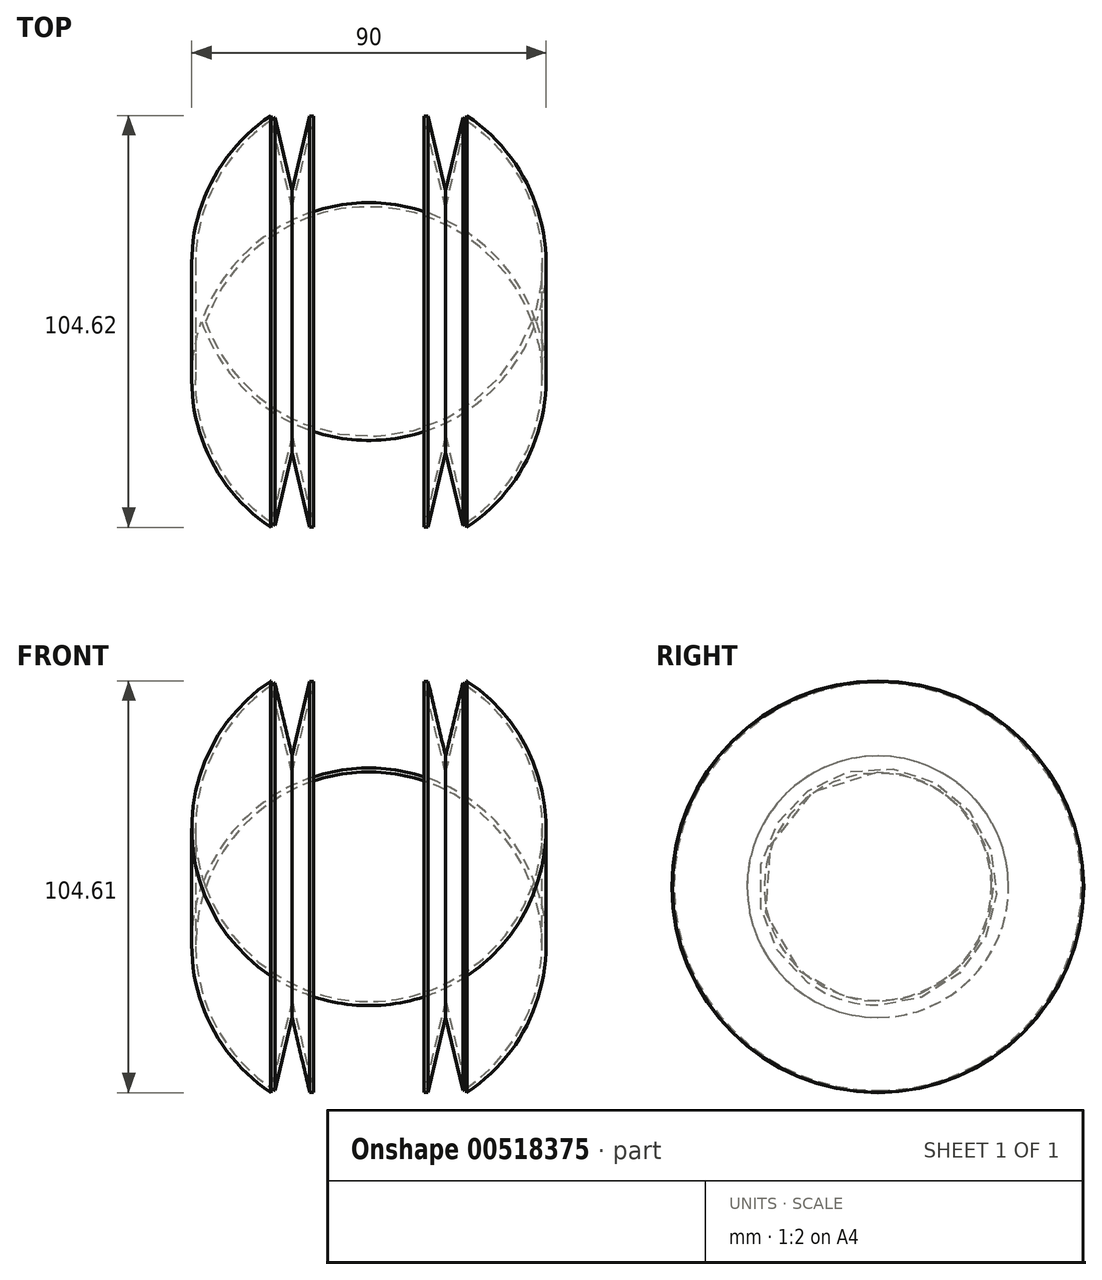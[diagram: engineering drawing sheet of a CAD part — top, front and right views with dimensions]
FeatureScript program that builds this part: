
annotation { "Feature Type Name" : "Feature", "Feature Type Description" : "" }
export const myFeature = defineFeature(function(context is Context, id is Id, definition is map)
    precondition{}
    {
        {
            var Q0;
            Q0=qCreatedBy(makeId("Front.planeOp"),FACE);
            var sketch = newSketch(context, id + "F0", { "sketchPlane" : qUnion([Q0])});
            skLineSegment(sketch, "E0", {"start": v(-25, 0) * mm, "end": v(0, 16.58) * mm});
            skLineSegment(sketch, "E1", {"start": v(0, 16.58) * mm, "end": v(25, 0) * mm});
            skLineSegment(sketch, "E2", {"start": v(25, 0) * mm, "end": v(19.5, -23.36) * mm});
            skLineSegment(sketch, "E3", {"start": v(19.5, -23.36) * mm, "end": v(14, 0) * mm});
            skLineSegment(sketch, "E4", {"start": v(14, 0) * mm, "end": v(-14, 0) * mm});
            skLineSegment(sketch, "E5", {"start": v(-14, 0) * mm, "end": v(-19.5, -23.36) * mm});
            skLineSegment(sketch, "E6", {"start": v(-19.5, -23.36) * mm, "end": v(-25, 0) * mm});
            skSolve(sketch);
        }
        {
            var Q0;
            Q0=qCreatedBy(makeId("Front.planeOp"),FACE);
            var sketch = newSketch(context, id + "F1", { "sketchPlane" : qUnion([Q0])});
            skLineSegment(sketch, "E7", {"start": v(0, 0) * mm, "end": v(0, -52.22) * mm});
            skLineSegment(sketch, "E8", {"start": v(0, -52.22) * mm, "end": v(-15.71, -52.22) * mm});
            skLineSegment(sketch, "E9", {"start": v(0, -52.22) * mm, "end": v(17.9, -52.22) * mm});
            skSolve(sketch);
        }
        {
            var Q0;
            Q0=qSketchRegion(id+"F0",true);
            var Q1;
            Q1=sQuery(id+"F1.wireOp",EDGE,"E9");
            revolve(context, id + "F2", {"entities" : qUnion([Q0]), "axis" : qUnion([Q1]), "revolveType" : RevolveType.FULL});
        }
        {
            var Q0;
            Q0=makeQuery(id+"F2.opRevolve","SWEPT_EDGE",EDGE,{"disambiguationData":[OSD([sQuery(id+"F0.wireOp",EDGE,"E0"),sQuery(id+"F0.wireOp",EDGE,"E1")])]});
            fillet(context, id + "F3", {"entities" : qUnion([Q0]), "radius" : 45 * mm, "tangentPropagation" : true, "allowEdgeOverflow" : false});
        }
        {
            var Q0;
            Q0=makeQuery(id+"F2.opRevolve","SWEPT_FACE",FACE,{"disambiguationData":[OSD([sQuery(id+"F0.wireOp",EDGE,"E4")])]});
            shell(context, id + "F4", {"entities" : qUnion([Q0]), "thickness" : 1 * mm});
        }
    });
